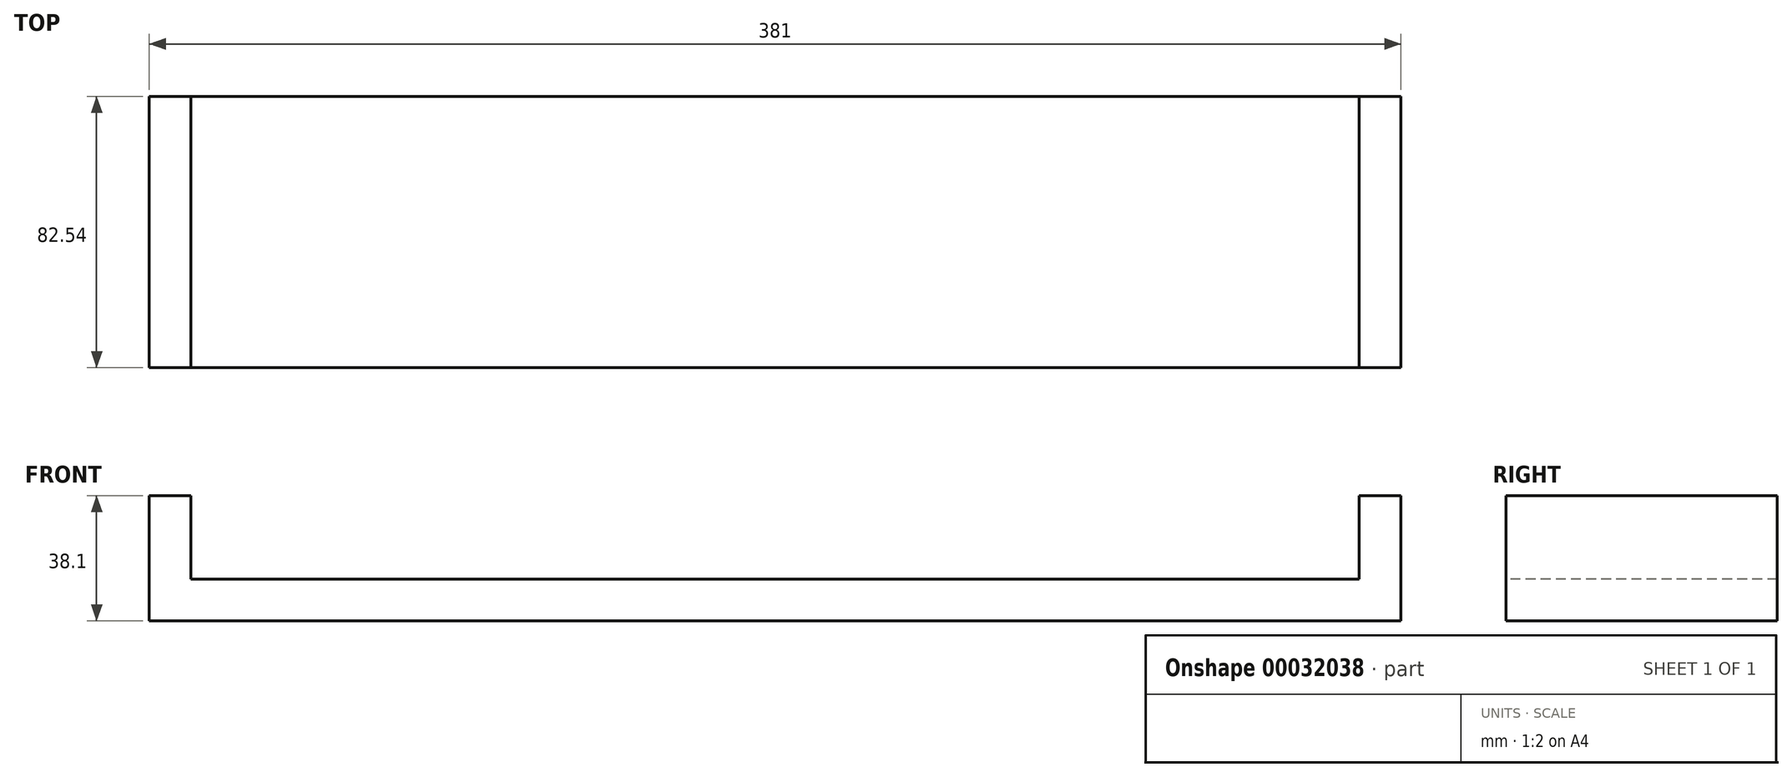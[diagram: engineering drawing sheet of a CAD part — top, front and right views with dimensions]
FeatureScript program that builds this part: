
annotation { "Feature Type Name" : "Feature", "Feature Type Description" : "" }
export const myFeature = defineFeature(function(context is Context, id is Id, definition is map)
    precondition{}
    {
        {
            var Q0;
            Q0=qCreatedBy(makeId("Top.planeOp"),FACE);
            var sketch = newSketch(context, id + "F0", { "sketchPlane" : qUnion([Q0])});
            skLineSegment(sketch, "E0.rect.bottom", {"start": v(190.5, 41.28) * mm, "end": v(-190.5, 41.28) * mm});
            skLineSegment(sketch, "E0.rect.top", {"start": v(190.5, -41.28) * mm, "end": v(-190.5, -41.28) * mm});
            skLineSegment(sketch, "E0.rect.left", {"start": v(190.5, 41.28) * mm, "end": v(190.5, -41.28) * mm});
            skLineSegment(sketch, "E0.rect.right", {"start": v(-190.5, 41.28) * mm, "end": v(-190.5, -41.28) * mm});
            skPoint(sketch, "E0.rect.middle", {"position": v(0, 0) * mm});
            skSolve(sketch);
        }
        {
            var Q0;
            Q0=makeQuery(id+"F0.imprint","IMPRINT",FACE,{"disambiguationData":[TD([[makeQuery(id+"F0.imprint","IMPRINT",EDGE,{"derivedFrom":sQuery(id+"F0.wireOp",EDGE,"E0.rect.bottom")}),1.0]])]});
            extrude(context, id + "F1", {"entities" : qUnion([Q0]), "depth" : 12.7 * mm});
        }
        {
            var Q0;
            Q0=makeQuery(id+"F1.opExtrude","CAP_FACE",FACE,{"disambiguationData":[OSD([sQuery(id+"F0.wireOp",EDGE,"E0.rect.bottom"),sQuery(id+"F0.wireOp",EDGE,"E0.rect.top"),sQuery(id+"F0.wireOp",EDGE,"E0.rect.left"),sQuery(id+"F0.wireOp",EDGE,"E0.rect.right")])],"isStart":false});
            var sketch = newSketch(context, id + "F2", { "sketchPlane" : qUnion([Q0])});
            skLineSegment(sketch, "E1.bottom", {"start": v(-190.5, -41.28) * mm, "end": v(-177.8, -41.28) * mm});
            skLineSegment(sketch, "E1.top", {"start": v(-190.5, 41.28) * mm, "end": v(-177.8, 41.28) * mm});
            skLineSegment(sketch, "E1.left", {"start": v(-190.5, -41.28) * mm, "end": v(-190.5, 41.28) * mm});
            skLineSegment(sketch, "E1.right", {"start": v(-177.8, -41.28) * mm, "end": v(-177.8, 41.28) * mm});
            skLineSegment(sketch, "E2.bottom", {"start": v(190.5, 41.28) * mm, "end": v(177.8, 41.28) * mm});
            skLineSegment(sketch, "E2.top", {"start": v(190.5, -41.28) * mm, "end": v(177.8, -41.28) * mm});
            skLineSegment(sketch, "E2.left", {"start": v(190.5, 41.28) * mm, "end": v(190.5, -41.28) * mm});
            skLineSegment(sketch, "E2.right", {"start": v(177.8, 41.28) * mm, "end": v(177.8, -41.28) * mm});
            skSolve(sketch);
        }
        {
            var Q0;
            Q0=makeQuery(id+"F2.imprint","IMPRINT",FACE,{"disambiguationData":[TD([[makeQuery(id+"F2.imprint","IMPRINT",EDGE,{"derivedFrom":sQuery(id+"F2.wireOp",EDGE,"E1.bottom")}),-1.0]])]});
            var Q1;
            Q1=makeQuery(id+"F2.imprint","IMPRINT",FACE,{"disambiguationData":[TD([[makeQuery(id+"F2.imprint","IMPRINT",EDGE,{"derivedFrom":sQuery(id+"F2.wireOp",EDGE,"E2.bottom")}),1.0]])]});
            extrude(context, id + "F3", {"entities" : qUnion([Q0, Q1]), "operationType" : NewBodyOperationType.ADD, "depth" : 25.4 * mm});
        }
    });
